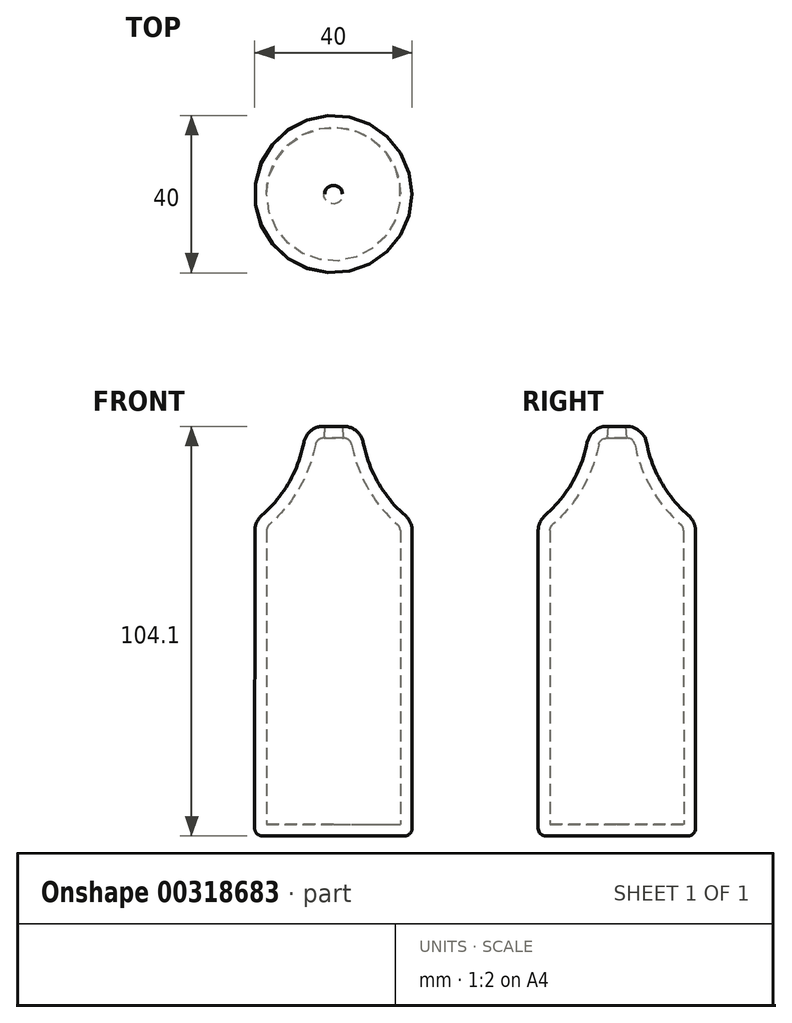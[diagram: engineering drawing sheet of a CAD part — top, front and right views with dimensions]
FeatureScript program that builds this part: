
annotation { "Feature Type Name" : "Feature", "Feature Type Description" : "" }
export const myFeature = defineFeature(function(context is Context, id is Id, definition is map)
    precondition{}
    {
        {
            var Q0;
            Q0=qCreatedBy(makeId("Front.planeOp"),FACE);
            var sketch = newSketch(context, id + "F0", { "sketchPlane" : qUnion([Q0])});
            skLineSegment(sketch, "E0.top", {"start": v(0, -60) * mm, "end": v(18, -60) * mm});
            skLineSegment(sketch, "E0.right", {"start": v(20, 20) * mm, "end": v(20, -58) * mm});
            skPoint(sketch, "E1.visualSharp", {"position": v(20, -60) * mm});
            skArc(sketch, "E1.filletArc", {"start": v(18, -60) * mm, "mid": v(19.41, -59.41) * mm, "end": v(20, -58) * mm});
            skPoint(sketch, "E2.endSnap0", {"position": v(0, -60) * mm});
            skArc(sketch, "E3.MirrorCS", {"start": v(20, 20) * mm, "mid": v(10.7, 31.04) * mm, "end": v(7, 45) * mm});
            skFitSpline(sketch, "E4", {"points": [v(-7, 45) * mm, v(-10, 47.5) * mm, v(0.03, 48.75) * mm, v(10, 47.5) * mm, v(7, 45) * mm, v(-7, 45) * mm]});
            skPoint(sketch, "E5.center.orphan", {"position": v(-40, 46.28) * mm});
            skPoint(sketch, "E0.left.start.orphan", {"position": v(-20, 20) * mm});
            skLineSegment(sketch, "E6", {"start": v(0.03, 48.75) * mm, "end": v(0, -60) * mm});
            skSolve(sketch);
        }
        {
            var Q0;
            {var subQ1=sQuery(id+"F0.wireOp",EDGE,"E0.top");Q0=makeQuery(id+"F0.imprint","IMPRINT",FACE,{"disambiguationData":[TD([[makeQuery(id+"F0.imprint","IMPRINT",EDGE,{"derivedFrom":subQ1}),1.0]])]});}
            var Q1;
            {var subQ0=sQuery(id+"F0.wireOp",EDGE,"E3.MirrorCS");Q1=makeQuery(id+"F0.imprint","IMPRINT",FACE,{"disambiguationData":[TD([[makeQuery(id+"F0.imprint","IMPRINT",EDGE,{"derivedFrom":subQ0}),1.0]])]});}
            var Q2;
            Q2=sQuery(id+"F0.wireOp",EDGE,"E6");
            revolve(context, id + "F1", {"entities" : qUnion([Q0, Q1]), "axis" : qUnion([Q2]), "revolveType" : RevolveType.FULL});
        }
        {
            var Q0;
            Q0=makeQuery(id+"F1.opRevolve","SWEPT_EDGE",EDGE,{"disambiguationData":[OSD([sQuery(id+"F0.wireOp",EDGE,"E0.bottom"),sQuery(id+"F0.wireOp",EDGE,"E0.right"),sQuery(id+"F0.wireOp",EDGE,"E3.MirrorCS")])]});
            var Q1;
            Q1=makeQuery(id+"F1.opRevolve","SWEPT_EDGE",EDGE,{"disambiguationData":[OSD([sQuery(id+"F0.wireOp",EDGE,"E3.MirrorCS"),sQuery(id+"F0.wireOp",EDGE,"E4")])]});
            fillet(context, id + "F2", {"entities" : qUnion([Q0, Q1]), "radius" : 5 * mm, "tangentPropagation" : true, "allowEdgeOverflow" : false});
        }
        {
            var Q0;
            Q0=makeQuery(id+"F1.opRevolve","SWEPT_FACE",FACE,{"disambiguationData":[OSD([sQuery(id+"F0.wireOp",EDGE,"E4")])]});
            shell(context, id + "F3", {"entities" : qUnion([Q0]), "thickness" : 3 * mm});
        }
    });
